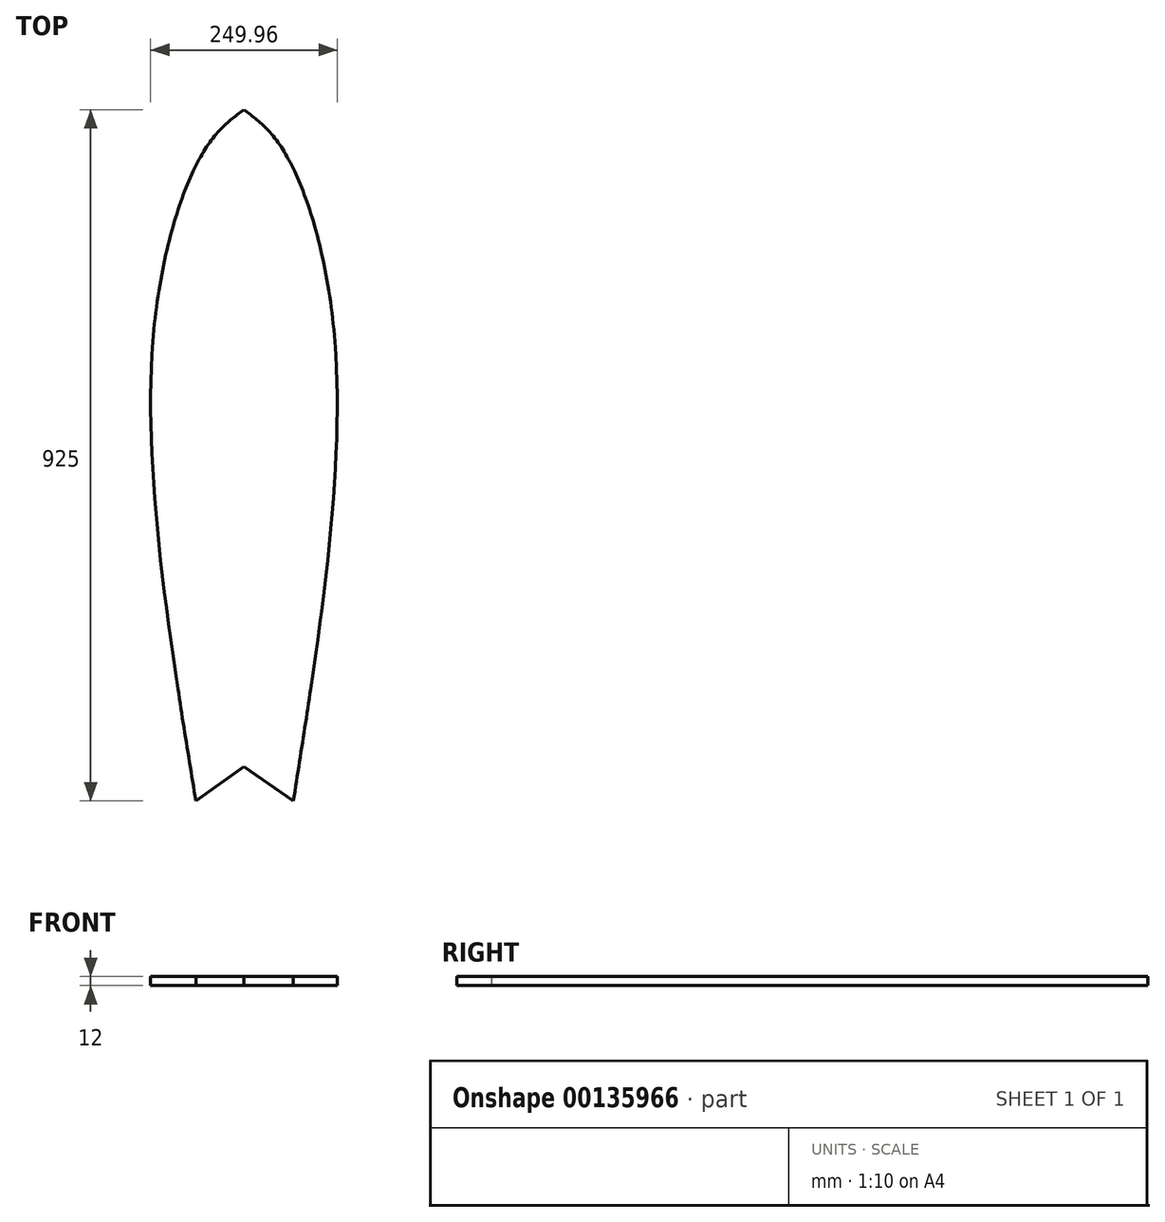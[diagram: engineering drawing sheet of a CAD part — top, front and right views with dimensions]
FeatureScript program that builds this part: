
annotation { "Feature Type Name" : "Feature", "Feature Type Description" : "" }
export const myFeature = defineFeature(function(context is Context, id is Id, definition is map)
    precondition{}
    {
        {
            var Q0;
            Q0=qCreatedBy(makeId("Top.planeOp"),FACE);
            var sketch = newSketch(context, id + "F0", { "sketchPlane" : qUnion([Q0])});
            skLineSegment(sketch, "E0", {"start": v(262.41, 0) * mm, "end": v(262.41, -925) * mm});
            skLineSegment(sketch, "E1", {"start": v(262.41, 0) * mm, "end": v(262.41, -50) * mm});
            skLineSegment(sketch, "E2", {"start": v(262.41, -50) * mm, "end": v(212.41, -50) * mm});
            skLineSegment(sketch, "E3", {"start": v(262.41, -50) * mm, "end": v(312.41, -50) * mm});
            skLineSegment(sketch, "E4", {"start": v(262.41, 0) * mm, "end": v(262.41, -310) * mm});
            skLineSegment(sketch, "E5", {"start": v(262.41, -310) * mm, "end": v(262.41, -925) * mm});
            skLineSegment(sketch, "E6", {"start": v(262.41, -310) * mm, "end": v(140.54, -310) * mm});
            skLineSegment(sketch, "E7", {"start": v(262.41, -310) * mm, "end": v(384.29, -310) * mm});
            skLineSegment(sketch, "E8", {"start": v(198, -925) * mm, "end": v(262.41, -878.83) * mm});
            skLineSegment(sketch, "E9", {"start": v(262.41, -878.83) * mm, "end": v(328.65, -925) * mm});
            skFitSpline(sketch, "E10", {"points": [v(262.41, 0) * mm, v(212.41, -50) * mm, v(140.54, -310) * mm, v(198, -925) * mm], "startDerivative": vector(-297.6, -222.4) * mm, "endDerivative": vector(213.65, -1319.91) * mm});
            skFitSpline(sketch, "E11", {"points": [v(262.41, 0) * mm, v(312.41, -50) * mm, v(384.29, -310) * mm, v(328.65, -925) * mm], "startDerivative": vector(297.7, -222.4) * mm, "endDerivative": vector(-208.85, -1320.04) * mm});
            skLineSegment(sketch, "E12", {"start": v(262.41, -150) * mm, "end": v(262.41, -775) * mm});
            skLineSegment(sketch, "E13", {"start": v(262.41, -775) * mm, "end": v(262.41, -925) * mm});
            skLineSegment(sketch, "E14", {"start": v(262.41, -775) * mm, "end": v(174.22, -775) * mm});
            skLineSegment(sketch, "E15", {"start": v(174.22, -775) * mm, "end": v(262.41, -775) * mm});
            skLineSegment(sketch, "E16", {"start": v(262.41, -775) * mm, "end": v(351.88, -775) * mm});
            skLineSegment(sketch, "E17", {"start": v(262.41, -150) * mm, "end": v(169.3, -150) * mm});
            skLineSegment(sketch, "E18", {"start": v(262.41, -150) * mm, "end": v(355.47, -150) * mm});
            skLineSegment(sketch, "E19", {"start": v(262.41, -150) * mm, "end": v(262.41, -310) * mm});
            skLineSegment(sketch, "E20", {"start": v(262.41, -150) * mm, "end": v(262.41, -50) * mm});
            skLineSegment(sketch, "E21", {"start": v(262.41, -310) * mm, "end": v(262.41, -775) * mm});
            skLineSegment(sketch, "E22", {"start": v(262.41, -775) * mm, "end": v(262.41, -878.83) * mm});
            skLineSegment(sketch, "E23", {"start": v(198, -925) * mm, "end": v(328.65, -925) * mm});
            skLineSegment(sketch, "E24", {"start": v(198, -925) * mm, "end": v(262.41, -925) * mm});
            skSolve(sketch);
        }
        {
            var Q0;
            {var subQ0=sQuery(id+"F0.wireOp",EDGE,"E2");Q0=makeQuery(id+"F0.imprint","IMPRINT",FACE,{"disambiguationData":[TD([[makeQuery(id+"F0.imprint","IMPRINT",EDGE,{"derivedFrom":subQ0}),-1.0]])]});}
            var Q1;
            {var subQ0=sQuery(id+"F0.wireOp",EDGE,"E3");Q1=makeQuery(id+"F0.imprint","IMPRINT",FACE,{"disambiguationData":[TD([[makeQuery(id+"F0.imprint","IMPRINT",EDGE,{"derivedFrom":subQ0}),1.0]])]});}
            var Q2;
            {var subQ1=sQuery(id+"F0.wireOp",EDGE,"E2");Q2=makeQuery(id+"F0.imprint","IMPRINT",FACE,{"disambiguationData":[TD([[makeQuery(id+"F0.imprint","IMPRINT",EDGE,{"derivedFrom":subQ1}),1.0]])]});}
            var Q3;
            {var subQ1=sQuery(id+"F0.wireOp",EDGE,"E3");Q3=makeQuery(id+"F0.imprint","IMPRINT",FACE,{"disambiguationData":[TD([[makeQuery(id+"F0.imprint","IMPRINT",EDGE,{"derivedFrom":subQ1}),-1.0]])]});}
            var Q4;
            {var subQ0=sQuery(id+"F0.wireOp",EDGE,"E6");Q4=makeQuery(id+"F0.imprint","IMPRINT",FACE,{"disambiguationData":[TD([[makeQuery(id+"F0.imprint","IMPRINT",EDGE,{"derivedFrom":subQ0}),1.0]])]});}
            var Q5;
            {var subQ0=sQuery(id+"F0.wireOp",EDGE,"E7");Q5=makeQuery(id+"F0.imprint","IMPRINT",FACE,{"disambiguationData":[TD([[makeQuery(id+"F0.imprint","IMPRINT",EDGE,{"derivedFrom":subQ0}),-1.0]])]});}
            var Q6;
            {var subQ0=sQuery(id+"F0.wireOp",EDGE,"E8");Q6=makeQuery(id+"F0.imprint","IMPRINT",FACE,{"disambiguationData":[TD([[makeQuery(id+"F0.imprint","IMPRINT",EDGE,{"derivedFrom":subQ0}),1.0]])]});}
            var Q7;
            {var subQ0=sQuery(id+"F0.wireOp",EDGE,"E9");Q7=makeQuery(id+"F0.imprint","IMPRINT",FACE,{"disambiguationData":[TD([[makeQuery(id+"F0.imprint","IMPRINT",EDGE,{"derivedFrom":subQ0}),1.0]])]});}
            var Q8;
            {var subQ0=sQuery(id+"F0.wireOp",EDGE,"E6");Q8=makeQuery(id+"F0.imprint","IMPRINT",FACE,{"disambiguationData":[TD([[makeQuery(id+"F0.imprint","IMPRINT",EDGE,{"derivedFrom":subQ0}),-1.0]])]});}
            var Q9;
            {var subQ0=sQuery(id+"F0.wireOp",EDGE,"E7");Q9=makeQuery(id+"F0.imprint","IMPRINT",FACE,{"disambiguationData":[TD([[makeQuery(id+"F0.imprint","IMPRINT",EDGE,{"derivedFrom":subQ0}),1.0]])]});}
            extrude(context, id + "F1", {"entities" : qUnion([Q0, Q1, Q2, Q3, Q4, Q5, Q6, Q7, Q8, Q9]), "depth" : 12 * mm});
        }
    });
